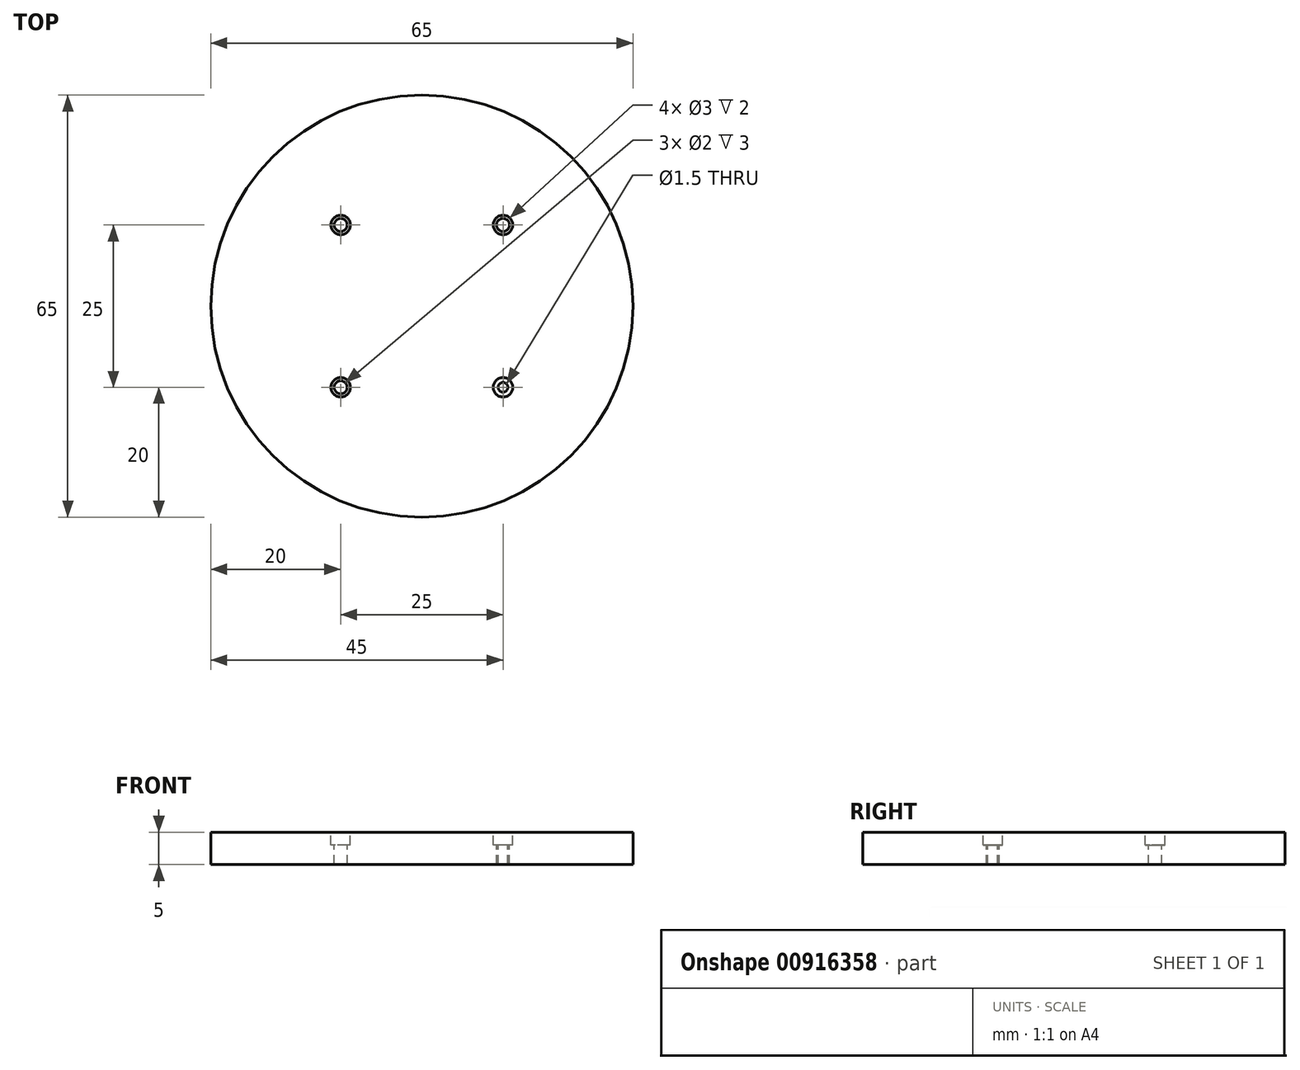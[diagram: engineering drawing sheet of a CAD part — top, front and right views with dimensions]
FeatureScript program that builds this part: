
annotation { "Feature Type Name" : "Feature", "Feature Type Description" : "" }
export const myFeature = defineFeature(function(context is Context, id is Id, definition is map)
    precondition{}
    {
        {
            var Q0;
            Q0=qCreatedBy(makeId("Top.planeOp"),FACE);
            var sketch = newSketch(context, id + "F0", { "sketchPlane" : qUnion([Q0])});
            skCircle(sketch, "E0", {"center": v(0, 0) * mm, "radius": 32.5 * mm});
            skSolve(sketch);
        }
        {
            var Q0;
            Q0=makeQuery(id+"F0.imprint","IMPRINT",FACE,{"disambiguationData":[TD([[makeQuery(id+"F0.imprint","IMPRINT",EDGE,{"derivedFrom":sQuery(id+"F0.wireOp",EDGE,"E0")}),1.0]])]});
            extrude(context, id + "F1", {"entities" : qUnion([Q0]), "depth" : 5 * mm, "offsetDistance" : 25 * mm});
        }
        {
            var Q0;
            Q0=qCreatedBy(makeId("Top.planeOp"),FACE);
            var sketch = newSketch(context, id + "F2", { "sketchPlane" : qUnion([Q0])});
            skLineSegment(sketch, "E1.bottom", {"start": v(12.5, 12.5) * mm, "end": v(-12.5, 12.5) * mm});
            skLineSegment(sketch, "E1.top", {"start": v(12.5, -12.5) * mm, "end": v(-12.5, -12.5) * mm});
            skLineSegment(sketch, "E1.left", {"start": v(12.5, 12.5) * mm, "end": v(12.5, -12.5) * mm});
            skLineSegment(sketch, "E1.right", {"start": v(-12.5, 12.5) * mm, "end": v(-12.5, -12.5) * mm});
            skPoint(sketch, "E1.middle", {"position": v(0, 0) * mm});
            skSolve(sketch);
        }
        {
            var Q0;
            Q0=makeQuery(id+"F1.opExtrude","CAP_FACE",FACE,{"disambiguationData":[OSD([sQuery(id+"F0.wireOp",EDGE,"E0")])],"isStart":false});
            var sketch = newSketch(context, id + "F3", { "sketchPlane" : qUnion([Q0])});
            skCircle(sketch, "E2", {"center": v(12.5, 12.5) * mm, "radius": 1.5 * mm});
            skCircle(sketch, "E3", {"center": v(12.5, -12.5) * mm, "radius": 1.5 * mm});
            skCircle(sketch, "E4", {"center": v(-12.5, -12.5) * mm, "radius": 1.5 * mm});
            skCircle(sketch, "E5", {"center": v(-12.5, 12.5) * mm, "radius": 1.5 * mm});
            skSolve(sketch);
        }
        {
            var Q0;
            Q0=makeQuery(id+"F3.imprint","IMPRINT",FACE,{"disambiguationData":[TD([[makeQuery(id+"F3.imprint","IMPRINT",EDGE,{"derivedFrom":sQuery(id+"F3.wireOp",EDGE,"E2")}),-1.0]])]});
            var sketch = newSketch(context, id + "F4", { "sketchPlane" : qUnion([Q0])});
            skCircle(sketch, "E6", {"center": v(12.5, -12.5) * mm, "radius": 0.75 * mm});
            skCircle(sketch, "E7", {"center": v(-12.5, 12.5) * mm, "radius": 1 * mm});
            skCircle(sketch, "E8", {"center": v(-12.5, -12.5) * mm, "radius": 1 * mm});
            skCircle(sketch, "E9", {"center": v(12.5, 12.5) * mm, "radius": 1 * mm});
            skSolve(sketch);
        }
        {
            var Q0;
            Q0 = qSketchRegion(id + "F4", true);
            extrude(context, id + "F5", {"entities" : qUnion([Q0]), "operationType" : NewBodyOperationType.REMOVE, "oppositeDirection" : true, "depth" : 5 * mm, "offsetDistance" : 25 * mm});
        }
        {
            var Q0;
            Q0 = qSketchRegion(id + "F3", true);
            extrude(context, id + "F6", {"entities" : qUnion([Q0]), "operationType" : NewBodyOperationType.REMOVE, "oppositeDirection" : true, "depth" : 2 * mm, "offsetDistance" : 25 * mm});
        }
    });
